# Revit family: 01-Torneira de mesa com regulador de tempo Bacteria-free para lavatorio - Pressmatic Deluxe - DocolMatic
name_source: partatom
category: Conexões hidráulicas
revit_build: Autodesk Revit MEP 2014 (Build: 20131024_2115(x64)
units: mm (PartAtom-declared; Revit-internal decimal feet)

## types (1)
- 1/2"
    Conexão CW = Sim
    Conexão HW = Sim
    Conexão de resíduos = Sim
    Conexão de ventilação = Sim
    Descrição = Torneira de mesa com regulador de tempo Bacteria-free 1/2" para lavatório, Pressmatic Deluxe - DocolMatic
    Diâmetro Nominal = 20  [stored 0.0656168 ft]
    Docol: Acabamento = Cromado
    Docol: Ambiente = Banheiro
    Docol: Bitola = 1/2"
    Docol: Categoria = Torneiras
    Docol: Código = 00773838
    Docol: Descrição = Torneira de mesa com regulador de tempo Bacteria-free 1/2" para lavatório, Pressmatic Deluxe - DocolMatic
    Docol: Fabricante = Docol
    Docol: Linha = Pressmatic
    Docol: Link do Produto = http://www.docol.com.br
    Elevação-padrão = 500  [stored 1.64042 ft]
    Fabricante = Docol
    Modelo = 00773838
    Raio Nominal = 10  [stored 0.0328084 ft]
    URL = www.docol.com.br

note: [stored X ft] marks values corroborated as IEEE doubles in the binary element streams (Revit-internal decimal feet)

## geometry (parser evidence)
native form markers: Sweep x1
no freeform markers — native parametric forms only
